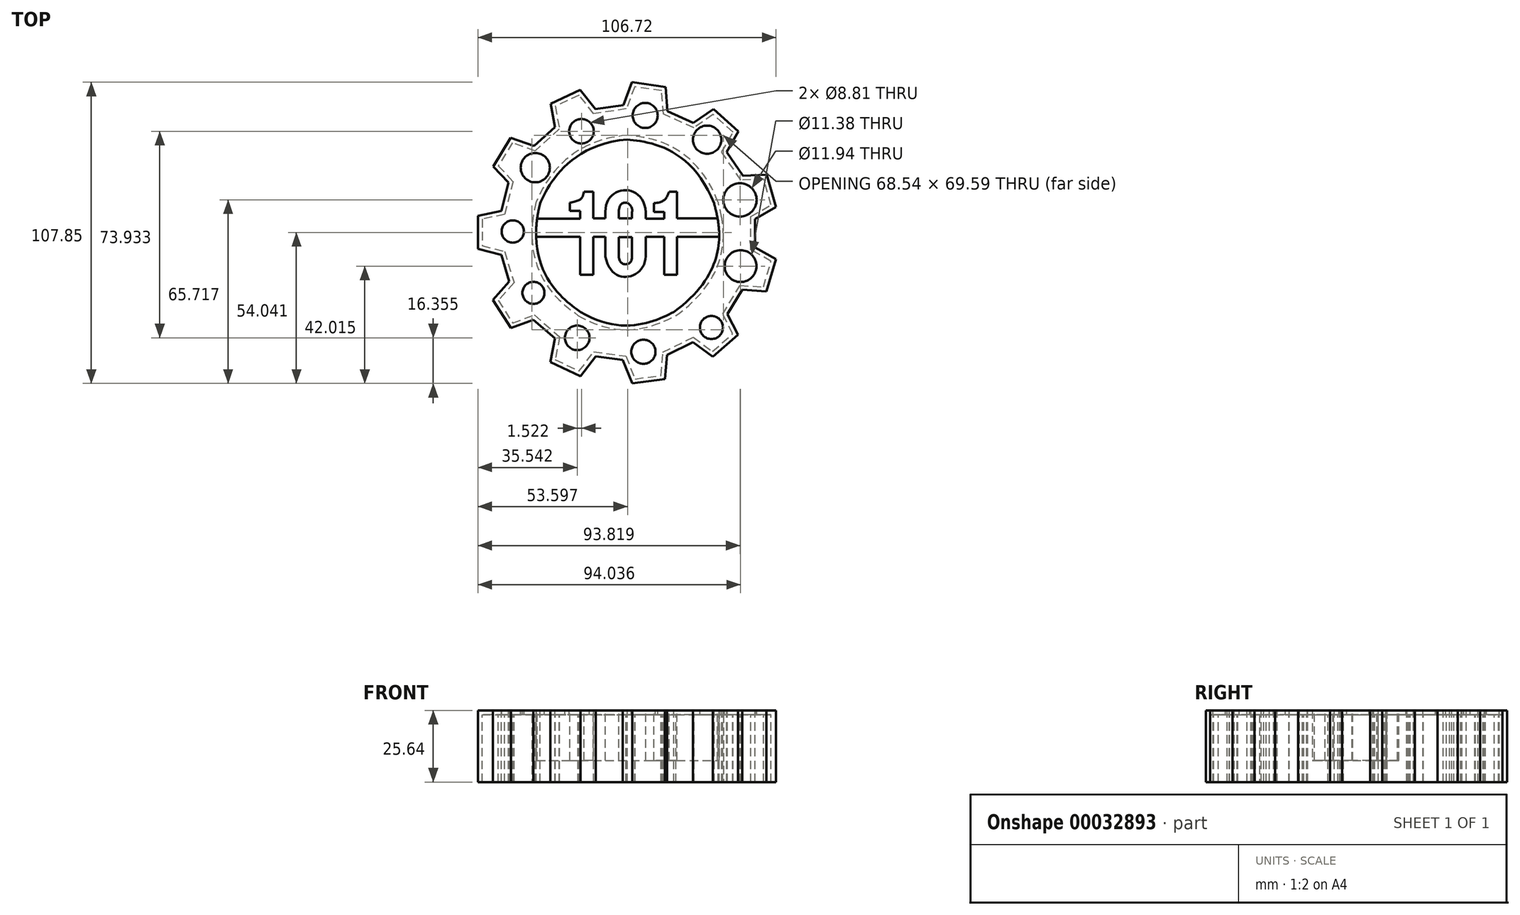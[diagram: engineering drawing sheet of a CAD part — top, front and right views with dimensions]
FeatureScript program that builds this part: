
annotation { "Feature Type Name" : "Feature", "Feature Type Description" : "" }
export const myFeature = defineFeature(function(context is Context, id is Id, definition is map)
    precondition{}
    {
        {
            var Q0;
            Q0=qCreatedBy(makeId("Top.planeOp"),FACE);
            var sketch = newSketch(context, id + "F0", { "sketchPlane" : qUnion([Q0])});
            skLineSegment(sketch, "E0", {"start": v(-41.7, 37.15) * mm, "end": v(-48, 26.88) * mm});
            skLineSegment(sketch, "E1", {"start": v(-48, 26.88) * mm, "end": v(-42.5, 21.05) * mm});
            skLineSegment(sketch, "E2", {"start": v(-42.5, 21.05) * mm, "end": v(-45.08, 10.98) * mm});
            skLineSegment(sketch, "E3", {"start": v(-45.08, 10.98) * mm, "end": v(-53.44, 9.22) * mm});
            skLineSegment(sketch, "E4", {"start": v(-53.44, 9.22) * mm, "end": v(-53.44, -2.68) * mm});
            skLineSegment(sketch, "E5", {"start": v(-53.44, -2.68) * mm, "end": v(-45.08, -4.8) * mm});
            skLineSegment(sketch, "E6", {"start": v(-45.08, -4.8) * mm, "end": v(-42.17, -14.33) * mm});
            skLineSegment(sketch, "E7", {"start": v(-42.17, -14.33) * mm, "end": v(-48.03, -20.95) * mm});
            skLineSegment(sketch, "E8", {"start": v(-48.03, -20.95) * mm, "end": v(-41.58, -30.99) * mm});
            skLineSegment(sketch, "E9", {"start": v(-41.58, -30.99) * mm, "end": v(-33.57, -28.03) * mm});
            skLineSegment(sketch, "E10", {"start": v(-33.57, -28.03) * mm, "end": v(-25.84, -34.66) * mm});
            skLineSegment(sketch, "E11", {"start": v(-25.84, -34.66) * mm, "end": v(-27.49, -43.18) * mm});
            skLineSegment(sketch, "E12", {"start": v(-27.49, -43.18) * mm, "end": v(-16.72, -48.25) * mm});
            skLineSegment(sketch, "E13", {"start": v(-16.72, -48.25) * mm, "end": v(-11.3, -41.1) * mm});
            skLineSegment(sketch, "E14", {"start": v(-11.3, -41.1) * mm, "end": v(-1.53, -42.39) * mm});
            skLineSegment(sketch, "E15", {"start": v(-1.53, -42.39) * mm, "end": v(1.84, -50.83) * mm});
            skLineSegment(sketch, "E16", {"start": v(1.84, -50.83) * mm, "end": v(13.53, -49.27) * mm});
            skLineSegment(sketch, "E17", {"start": v(13.53, -49.27) * mm, "end": v(14.22, -40.58) * mm});
            skLineSegment(sketch, "E18", {"start": v(14.22, -40.58) * mm, "end": v(23.54, -36.01) * mm});
            skLineSegment(sketch, "E19", {"start": v(23.54, -36.01) * mm, "end": v(30.6, -41.27) * mm});
            skLineSegment(sketch, "E20", {"start": v(30.6, -41.27) * mm, "end": v(39.68, -33.4) * mm});
            skLineSegment(sketch, "E21", {"start": v(39.68, -33.4) * mm, "end": v(35.88, -26.06) * mm});
            skLineSegment(sketch, "E22", {"start": v(35.88, -26.06) * mm, "end": v(41.2, -17.3) * mm});
            skLineSegment(sketch, "E23", {"start": v(41.2, -17.3) * mm, "end": v(49.87, -17.83) * mm});
            skLineSegment(sketch, "E24", {"start": v(49.87, -17.83) * mm, "end": v(53.28, -6.33) * mm});
            skLineSegment(sketch, "E25", {"start": v(53.28, -6.33) * mm, "end": v(45.8, -2.09) * mm});
            skLineSegment(sketch, "E26", {"start": v(45.8, -2.09) * mm, "end": v(45.8, 8.02) * mm});
            skLineSegment(sketch, "E27", {"start": v(45.8, 8.02) * mm, "end": v(53.28, 12.35) * mm});
            skLineSegment(sketch, "E28", {"start": v(53.28, 12.35) * mm, "end": v(49.97, 23.95) * mm});
            skLineSegment(sketch, "E29", {"start": v(49.97, 23.95) * mm, "end": v(41.47, 23.51) * mm});
            skLineSegment(sketch, "E30", {"start": v(41.47, 23.51) * mm, "end": v(35.6, 32.1) * mm});
            skLineSegment(sketch, "E31", {"start": v(35.6, 32.1) * mm, "end": v(39.78, 39.42) * mm});
            skLineSegment(sketch, "E32", {"start": v(39.78, 39.42) * mm, "end": v(30.88, 47.38) * mm});
            skLineSegment(sketch, "E33", {"start": v(30.88, 47.38) * mm, "end": v(23.71, 42.42) * mm});
            skLineSegment(sketch, "E34", {"start": v(23.71, 42.42) * mm, "end": v(14.41, 46.58) * mm});
            skLineSegment(sketch, "E35", {"start": v(14.41, 46.58) * mm, "end": v(13.79, 55.33) * mm});
            skLineSegment(sketch, "E36", {"start": v(13.79, 55.33) * mm, "end": v(1.69, 57.02) * mm});
            skLineSegment(sketch, "E37", {"start": v(1.69, 57.02) * mm, "end": v(-1.36, 48.84) * mm});
            skLineSegment(sketch, "E38", {"start": v(-1.36, 48.84) * mm, "end": v(-11.35, 47.38) * mm});
            skLineSegment(sketch, "E39", {"start": v(-11.35, 47.38) * mm, "end": v(-16.84, 54.28) * mm});
            skLineSegment(sketch, "E40", {"start": v(-16.84, 54.28) * mm, "end": v(-27.43, 49.25) * mm});
            skLineSegment(sketch, "E41", {"start": v(-27.43, 49.25) * mm, "end": v(-25.9, 40.89) * mm});
            skLineSegment(sketch, "E42", {"start": v(-25.9, 40.89) * mm, "end": v(-33.3, 34.14) * mm});
            skLineSegment(sketch, "E43", {"start": v(-33.3, 34.14) * mm, "end": v(-41.7, 37.15) * mm});
            skLineSegment(sketch, "E44", {"start": v(-20.54, 13.91) * mm, "end": v(-20.54, 10.91) * mm});
            skLineSegment(sketch, "E45", {"start": v(-20.54, 10.91) * mm, "end": v(-16.86, 10.91) * mm});
            skLineSegment(sketch, "E46", {"start": v(-16.86, 10.91) * mm, "end": v(-16.86, -11.97) * mm});
            skLineSegment(sketch, "E47", {"start": v(-16.86, -11.97) * mm, "end": v(-12.16, -11.97) * mm});
            skLineSegment(sketch, "E48", {"start": v(-12.16, -11.97) * mm, "end": v(-12.16, 17.82) * mm});
            skLineSegment(sketch, "E49", {"start": v(-12.16, 17.82) * mm, "end": v(-15.44, 17.82) * mm});
            skLineSegment(sketch, "E50", {"start": v(15, 17.82) * mm, "end": v(17.82, 17.82) * mm});
            skLineSegment(sketch, "E51", {"start": v(17.82, 17.82) * mm, "end": v(17.82, -11.97) * mm});
            skLineSegment(sketch, "E52", {"start": v(17.82, -11.97) * mm, "end": v(13.32, -11.97) * mm});
            skLineSegment(sketch, "E53", {"start": v(13.32, -11.97) * mm, "end": v(13.32, 10.6) * mm});
            skLineSegment(sketch, "E54", {"start": v(13.32, 10.6) * mm, "end": v(9.57, 10.6) * mm});
            skLineSegment(sketch, "E55", {"start": v(9.57, 10.6) * mm, "end": v(9.57, 13.7) * mm});
            skLineSegment(sketch, "E56", {"start": v(-3.02, 10.49) * mm, "end": v(-3.02, -5.23) * mm});
            skLineSegment(sketch, "E57", {"start": v(1.72, 10.46) * mm, "end": v(1.72, -5.12) * mm});
            skLineSegment(sketch, "E58", {"start": v(-7.8, 10.68) * mm, "end": v(-7.8, -5.38) * mm});
            skLineSegment(sketch, "E59", {"start": v(6.64, 10.5) * mm, "end": v(6.64, -5.32) * mm});
            skFitSpline(sketch, "E60", {"points": [v(0, 36.5) * mm, v(-31.17, 13.6) * mm], "startDerivative": vector(-66.75, -5.35) * mm, "endDerivative": vector(-5.35, -12.5) * mm});
            skFitSpline(sketch, "E61", {"points": [v(-31.17, 13.6) * mm, v(-16.75, -25.22) * mm], "startDerivative": vector(-19.63, -78.08) * mm, "endDerivative": vector(9.82, -8.03) * mm});
            skFitSpline(sketch, "E62", {"points": [v(-16.75, -25.22) * mm, v(16.71, -25.22) * mm], "startDerivative": vector(45.95, -27.22) * mm, "endDerivative": vector(19.63, 9.82) * mm});
            skFitSpline(sketch, "E63", {"points": [v(16.71, -25.22) * mm, v(31.14, 13.6) * mm], "startDerivative": vector(63.36, 45.95) * mm, "endDerivative": vector(-5.35, 20.97) * mm});
            skFitSpline(sketch, "E64", {"points": [v(31.14, 13.6) * mm, v(0, 36.5) * mm], "startDerivative": vector(-24.1, 61.12) * mm, "endDerivative": vector(-23.38, 2.23) * mm});
            skFitSpline(sketch, "E65", {"points": [v(-7.8, 10.68) * mm, v(6.64, 10.5) * mm], "startDerivative": vector(-0.47, 28.74) * mm, "endDerivative": vector(1.88, -33.22) * mm});
            skFitSpline(sketch, "E66", {"points": [v(-7.8, -5.38) * mm, v(6.64, -5.32) * mm], "startDerivative": vector(5.8, -33.2) * mm, "endDerivative": vector(0.82, 25.1) * mm});
            skFitSpline(sketch, "E67", {"points": [v(-3.02, -5.23) * mm, v(1.72, -5.12) * mm], "startDerivative": vector(0.37, -12.33) * mm, "endDerivative": vector(-1.45, 11.56) * mm});
            skFitSpline(sketch, "E68", {"points": [v(-3.02, 10.49) * mm, v(1.72, 10.46) * mm], "startDerivative": vector(0.1, 16.48) * mm, "endDerivative": vector(-2.2, -10.92) * mm});
            skFitSpline(sketch, "E69", {"points": [v(-20.54, 13.91) * mm, v(-15.44, 17.82) * mm], "startDerivative": vector(14.58, 2.27) * mm, "endDerivative": vector(2.06, 6.02) * mm});
            skFitSpline(sketch, "E70", {"points": [v(9.57, 13.7) * mm, v(15, 17.82) * mm], "startDerivative": vector(13.62, 1.18) * mm, "endDerivative": vector(2.38, 5.46) * mm});
            skLineSegment(sketch, "E71", {"start": v(-32.23, 8.2) * mm, "end": v(-16.86, 8.2) * mm});
            skLineSegment(sketch, "E72", {"start": v(-32.6, 1.63) * mm, "end": v(-16.86, 1.63) * mm});
            skLineSegment(sketch, "E73", {"start": v(-12.16, 1.72) * mm, "end": v(-7.8, 1.72) * mm});
            skLineSegment(sketch, "E74", {"start": v(-12.16, 8.23) * mm, "end": v(-7.8, 8.23) * mm});
            skLineSegment(sketch, "E75", {"start": v(-3.02, 8.23) * mm, "end": v(1.72, 8.23) * mm});
            skLineSegment(sketch, "E76", {"start": v(-3.02, 1.55) * mm, "end": v(1.72, 1.55) * mm});
            skLineSegment(sketch, "E77", {"start": v(6.64, 1.72) * mm, "end": v(13.32, 1.72) * mm});
            skLineSegment(sketch, "E78", {"start": v(6.64, 8.14) * mm, "end": v(13.32, 8.14) * mm});
            skLineSegment(sketch, "E79", {"start": v(17.82, 8.23) * mm, "end": v(32.37, 8.23) * mm});
            skPoint(sketch, "E79.startSnap0", {"position": v(-0.65, 8.23) * mm});
            skLineSegment(sketch, "E80", {"start": v(17.82, 1.72) * mm, "end": v(32.93, 1.72) * mm});
            skSolve(sketch);
        }
        {
            var Q0;
            Q0=makeQuery(id+"F0.imprint","IMPRINT",FACE,{"disambiguationData":[TD([[makeQuery(id+"F0.imprint","IMPRINT",EDGE,{"derivedFrom":sQuery(id+"F0.wireOp",EDGE,"E0")}),1.0]])]});
            extrude(context, id + "F1", {"entities" : qUnion([Q0]), "oppositeDirection" : true, "depth" : 25.64 * mm});
        }
        {
            var Q0;
            Q0=makeQuery(id+"F1.opExtrude","CAP_FACE",FACE,{"disambiguationData":[OSD([sQuery(id+"F0.wireOp",EDGE,"E0"),sQuery(id+"F0.wireOp",EDGE,"E1"),sQuery(id+"F0.wireOp",EDGE,"E2"),sQuery(id+"F0.wireOp",EDGE,"E3"),sQuery(id+"F0.wireOp",EDGE,"E4"),sQuery(id+"F0.wireOp",EDGE,"E5"),sQuery(id+"F0.wireOp",EDGE,"E6"),sQuery(id+"F0.wireOp",EDGE,"E7"),sQuery(id+"F0.wireOp",EDGE,"E8"),sQuery(id+"F0.wireOp",EDGE,"E9"),sQuery(id+"F0.wireOp",EDGE,"E10"),sQuery(id+"F0.wireOp",EDGE,"E11"),sQuery(id+"F0.wireOp",EDGE,"E12"),sQuery(id+"F0.wireOp",EDGE,"E13"),sQuery(id+"F0.wireOp",EDGE,"E14"),sQuery(id+"F0.wireOp",EDGE,"E15"),sQuery(id+"F0.wireOp",EDGE,"E16"),sQuery(id+"F0.wireOp",EDGE,"E17"),sQuery(id+"F0.wireOp",EDGE,"E18"),sQuery(id+"F0.wireOp",EDGE,"E19"),sQuery(id+"F0.wireOp",EDGE,"E20"),sQuery(id+"F0.wireOp",EDGE,"E21"),sQuery(id+"F0.wireOp",EDGE,"E22"),sQuery(id+"F0.wireOp",EDGE,"E23"),sQuery(id+"F0.wireOp",EDGE,"E24"),sQuery(id+"F0.wireOp",EDGE,"E25"),sQuery(id+"F0.wireOp",EDGE,"E26"),sQuery(id+"F0.wireOp",EDGE,"E27"),sQuery(id+"F0.wireOp",EDGE,"E28"),sQuery(id+"F0.wireOp",EDGE,"E29"),sQuery(id+"F0.wireOp",EDGE,"E30"),sQuery(id+"F0.wireOp",EDGE,"E31"),sQuery(id+"F0.wireOp",EDGE,"E32"),sQuery(id+"F0.wireOp",EDGE,"E33"),sQuery(id+"F0.wireOp",EDGE,"E34"),sQuery(id+"F0.wireOp",EDGE,"E35"),sQuery(id+"F0.wireOp",EDGE,"E36"),sQuery(id+"F0.wireOp",EDGE,"E37"),sQuery(id+"F0.wireOp",EDGE,"E38"),sQuery(id+"F0.wireOp",EDGE,"E39"),sQuery(id+"F0.wireOp",EDGE,"E40"),sQuery(id+"F0.wireOp",EDGE,"E41"),sQuery(id+"F0.wireOp",EDGE,"E42"),sQuery(id+"F0.wireOp",EDGE,"E43"),sQuery(id+"F0.wireOp",EDGE,"E60"),sQuery(id+"F0.wireOp",EDGE,"E61"),sQuery(id+"F0.wireOp",EDGE,"E62"),sQuery(id+"F0.wireOp",EDGE,"E63"),sQuery(id+"F0.wireOp",EDGE,"E64")])],"isStart":false});
            shell(context, id + "F2", {"entities" : qUnion([Q0]), "thickness" : 1.5 * mm});
        }
        {
            var Q0;
            {var subQ1=sQuery(id+"F0.wireOp",EDGE,"E71");Q0=makeQuery(id+"F0.imprint","IMPRINT",FACE,{"disambiguationData":[TD([[makeQuery(id+"F0.imprint","IMPRINT",EDGE,{"derivedFrom":subQ1}),-1.0]])]});}
            var Q1;
            Q1=makeQuery(id+"F0.imprint","IMPRINT",FACE,{"disambiguationData":[TD([[makeQuery(id+"F0.imprint","IMPRINT",EDGE,{"derivedFrom":sQuery(id+"F0.wireOp",EDGE,"E44")}),1.0]])]});
            var Q2;
            {var subQ0=sQuery(id+"F0.wireOp",EDGE,"E73");Q2=makeQuery(id+"F0.imprint","IMPRINT",FACE,{"disambiguationData":[TD([[makeQuery(id+"F0.imprint","IMPRINT",EDGE,{"derivedFrom":subQ0}),1.0]])]});}
            var Q3;
            {var subQ1=sQuery(id+"F0.wireOp",EDGE,"E75");Q3=makeQuery(id+"F0.imprint","IMPRINT",FACE,{"disambiguationData":[TD([[makeQuery(id+"F0.imprint","IMPRINT",EDGE,{"derivedFrom":subQ1}),-1.0]])]});}
            var Q4;
            {var subQ2=sQuery(id+"F0.wireOp",EDGE,"E65");Q4=makeQuery(id+"F0.imprint","IMPRINT",FACE,{"disambiguationData":[TD([[makeQuery(id+"F0.imprint","IMPRINT",EDGE,{"derivedFrom":subQ2}),-1.0]])]});}
            var Q5;
            {var subQ0=sQuery(id+"F0.wireOp",EDGE,"E77");Q5=makeQuery(id+"F0.imprint","IMPRINT",FACE,{"disambiguationData":[TD([[makeQuery(id+"F0.imprint","IMPRINT",EDGE,{"derivedFrom":subQ0}),1.0]])]});}
            var Q6;
            {var subQ8=sQuery(id+"F0.wireOp",EDGE,"E50");Q6=makeQuery(id+"F0.imprint","IMPRINT",FACE,{"disambiguationData":[TD([[makeQuery(id+"F0.imprint","IMPRINT",EDGE,{"derivedFrom":subQ8}),-1.0]])]});}
            var Q7;
            {var subQ1=sQuery(id+"F0.wireOp",EDGE,"E79");Q7=makeQuery(id+"F0.imprint","IMPRINT",FACE,{"disambiguationData":[TD([[makeQuery(id+"F0.imprint","IMPRINT",EDGE,{"derivedFrom":subQ1}),-1.0]])]});}
            extrude(context, id + "F3", {"entities" : qUnion([Q0, Q1, Q2, Q3, Q4, Q5, Q6, Q7]), "oppositeDirection" : true, "depth" : 17.91 * mm});
        }
        {
            var Q0;
            Q0=makeQuery(id+"F0.imprint","IMPRINT",FACE,{"disambiguationData":[TD([[makeQuery(id+"F0.imprint","IMPRINT",EDGE,{"derivedFrom":sQuery(id+"F0.wireOp",EDGE,"E0")}),1.0]])]});
            var sketch = newSketch(context, id + "F4", { "sketchPlane" : qUnion([Q0])});
            skCircle(sketch, "E81", {"center": v(-40.95, 3.58) * mm, "radius": 4 * mm});
            skCircle(sketch, "E82", {"center": v(-33.55, -18.38) * mm, "radius": 3.94 * mm});
            skCircle(sketch, "E83", {"center": v(-17.9, -34.47) * mm, "radius": 4.4 * mm});
            skCircle(sketch, "E84", {"center": v(5.8, -39.48) * mm, "radius": 4.33 * mm});
            skCircle(sketch, "E85", {"center": v(30.16, -30.78) * mm, "radius": 4.13 * mm});
            skCircle(sketch, "E86", {"center": v(40.6, -8.82) * mm, "radius": 5.7 * mm});
            skCircle(sketch, "E87", {"center": v(40.38, 14.89) * mm, "radius": 5.97 * mm});
            skCircle(sketch, "E88", {"center": v(28.64, 36.41) * mm, "radius": 5.06 * mm});
            skCircle(sketch, "E89", {"center": v(6.46, 45.11) * mm, "radius": 4.48 * mm});
            skCircle(sketch, "E90", {"center": v(-16.38, 39.46) * mm, "radius": 4.4 * mm});
            skCircle(sketch, "E91", {"center": v(-32.9, 26.41) * mm, "radius": 5.23 * mm});
            skSolve(sketch);
        }
        {
            var Q0;
            Q0 = qSketchRegion(id + "F4", true);
            extrude(context, id + "F5", {"entities" : qUnion([Q0]), "operationType" : NewBodyOperationType.REMOVE, "oppositeDirection" : true, "depth" : 25 * mm});
        }
    });
